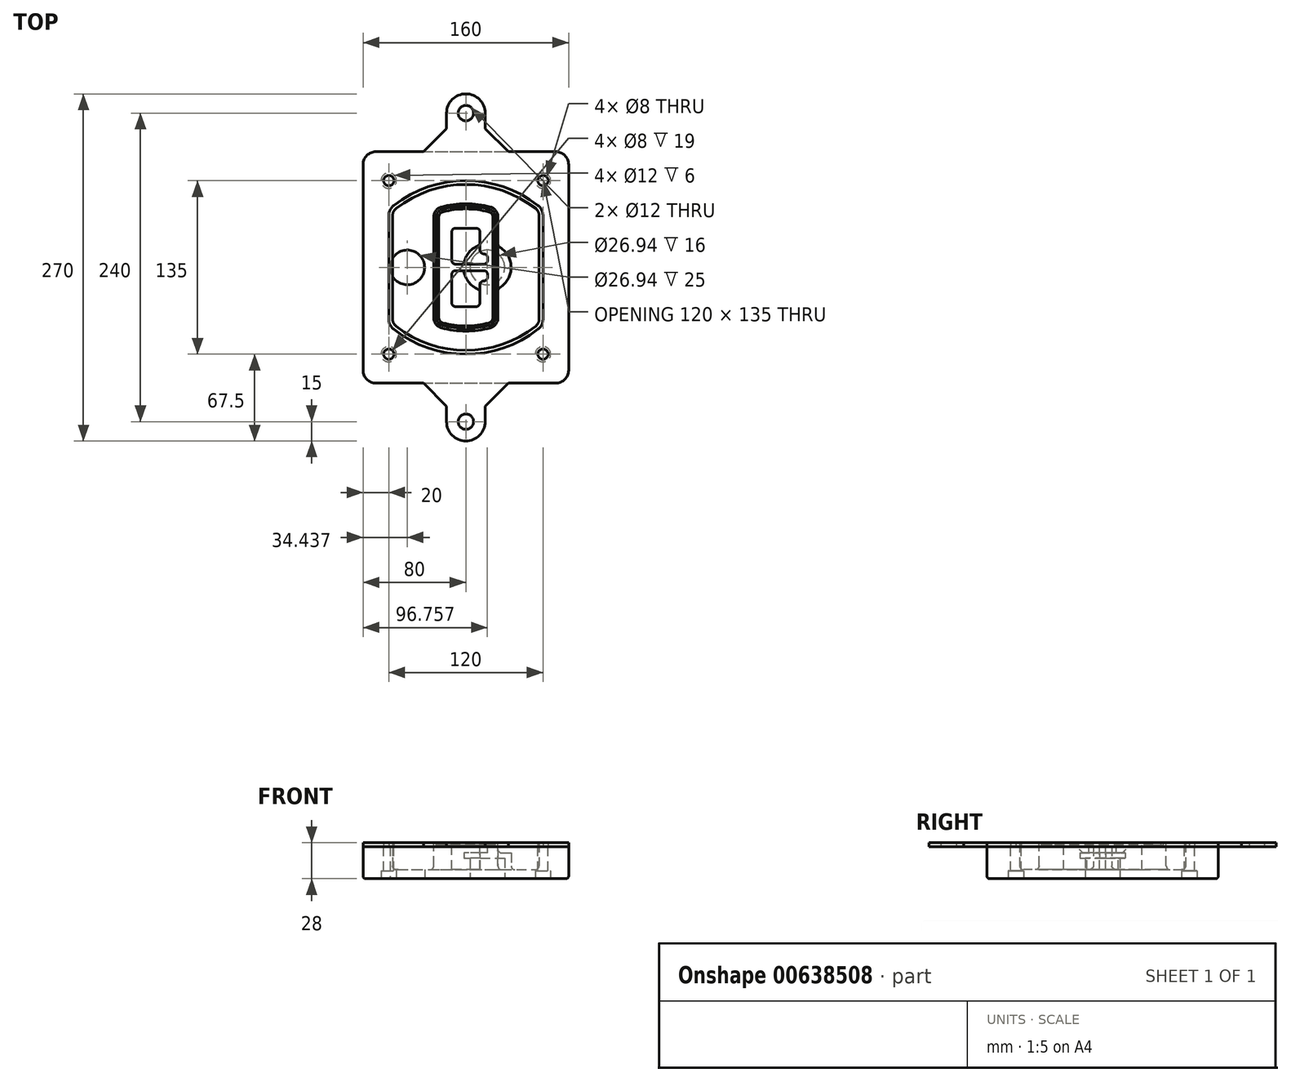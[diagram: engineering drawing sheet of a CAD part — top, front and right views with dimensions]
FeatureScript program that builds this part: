
annotation { "Feature Type Name" : "Feature", "Feature Type Description" : "" }
export const myFeature = defineFeature(function(context is Context, id is Id, definition is map)
    precondition{}
    {
        {
            var Q0;
            Q0=qCreatedBy(makeId("Top.planeOp"),FACE);
            var sketch = newSketch(context, id + "F0", { "sketchPlane" : qUnion([Q0])});
            skPoint(sketch, "E0.rect.middle", {"position": v(0, 0) * mm});
            skLineSegment(sketch, "E1.bottom", {"start": v(-70, -90) * mm, "end": v(70, -90) * mm});
            skLineSegment(sketch, "E1.top", {"start": v(-70, 90) * mm, "end": v(70, 90) * mm});
            skLineSegment(sketch, "E1.left", {"start": v(-80, -80) * mm, "end": v(-80, 80) * mm});
            skLineSegment(sketch, "E1.right", {"start": v(80, -80) * mm, "end": v(80, 80) * mm});
            skLineSegment(sketch, "E2", {"start": v(-80, 90) * mm, "end": v(80, -90) * mm, "construction": true});
            skLineSegment(sketch, "E3", {"start": v(80, 90) * mm, "end": v(-80, -90) * mm, "construction": true});
            skCircle(sketch, "E4", {"center": v(-60, 67.5) * mm, "radius": 4 * mm});
            skCircle(sketch, "E5", {"center": v(60, 67.5) * mm, "radius": 4 * mm});
            skCircle(sketch, "E6", {"center": v(60, -67.5) * mm, "radius": 4 * mm});
            skCircle(sketch, "E7", {"center": v(-60, -67.5) * mm, "radius": 4 * mm});
            skLineSegment(sketch, "E8", {"start": v(-60, 67.5) * mm, "end": v(60, 67.5) * mm, "construction": true});
            skLineSegment(sketch, "E9", {"start": v(60, 67.5) * mm, "end": v(60, -67.5) * mm, "construction": true});
            skLineSegment(sketch, "E10", {"start": v(60, -67.5) * mm, "end": v(-60, -67.5) * mm, "construction": true});
            skLineSegment(sketch, "E11", {"start": v(-60, -67.5) * mm, "end": v(-60, 67.5) * mm, "construction": true});
            skLineSegment(sketch, "E12", {"start": v(-60, 40.3) * mm, "end": v(-60, -40.3) * mm});
            skLineSegment(sketch, "E13", {"start": v(60, 40.3) * mm, "end": v(60, -40.3) * mm});
            skArc(sketch, "E14", {"start": v(56.15, 48.18) * mm, "mid": v(0, 67.5) * mm, "end": v(-56.15, 48.18) * mm});
            skArc(sketch, "E15", {"start": v(-56.15, -48.18) * mm, "mid": v(0, -67.5) * mm, "end": v(56.15, -48.18) * mm});
            skLineSegment(sketch, "E16", {"start": v(-60, 0) * mm, "end": v(60, 0) * mm, "construction": true});
            skPoint(sketch, "E17.visualSharp", {"position": v(-60, -45) * mm});
            skArc(sketch, "E17.filletArc", {"start": v(-60, -40.3) * mm, "mid": v(-58.99, -44.68) * mm, "end": v(-56.15, -48.18) * mm});
            skPoint(sketch, "E18.visualSharp", {"position": v(-60, 45) * mm});
            skArc(sketch, "E18.filletArc", {"start": v(-56.15, 48.18) * mm, "mid": v(-58.99, 44.68) * mm, "end": v(-60, 40.3) * mm});
            skPoint(sketch, "E19.visualSharp", {"position": v(60, 45) * mm});
            skArc(sketch, "E19.filletArc", {"start": v(60, 40.3) * mm, "mid": v(58.99, 44.68) * mm, "end": v(56.15, 48.18) * mm});
            skPoint(sketch, "E20.visualSharp", {"position": v(60, -45) * mm});
            skArc(sketch, "E20.filletArc", {"start": v(56.15, -48.18) * mm, "mid": v(58.99, -44.68) * mm, "end": v(60, -40.3) * mm});
            skPoint(sketch, "E21.visualSharp", {"position": v(-80, 90) * mm});
            skArc(sketch, "E21.filletArc", {"start": v(-70, 90) * mm, "mid": v(-77.07, 87.07) * mm, "end": v(-80, 80) * mm});
            skPoint(sketch, "E22.visualSharp", {"position": v(80, 90) * mm});
            skArc(sketch, "E22.filletArc", {"start": v(80, 80) * mm, "mid": v(77.07, 87.07) * mm, "end": v(70, 90) * mm});
            skPoint(sketch, "E23.visualSharp", {"position": v(80, -90) * mm});
            skArc(sketch, "E23.filletArc", {"start": v(70, -90) * mm, "mid": v(77.07, -87.07) * mm, "end": v(80, -80) * mm});
            skPoint(sketch, "E24.visualSharp", {"position": v(-80, -90) * mm});
            skArc(sketch, "E24.filletArc", {"start": v(-80, -80) * mm, "mid": v(-77.07, -87.07) * mm, "end": v(-70, -90) * mm});
            skArc(sketch, "E25.0", {"start": v(57, 40.3) * mm, "mid": v(56.3, 43.36) * mm, "end": v(54.3, 45.81) * mm});
            skLineSegment(sketch, "E25.1", {"start": v(57, 40.3) * mm, "end": v(57, -40.3) * mm});
            skArc(sketch, "E25.2", {"start": v(54.3, -45.81) * mm, "mid": v(56.3, -43.36) * mm, "end": v(57, -40.3) * mm});
            skArc(sketch, "E25.3", {"start": v(-54.3, -45.81) * mm, "mid": v(0, -64.5) * mm, "end": v(54.3, -45.81) * mm});
            skArc(sketch, "E25.4", {"start": v(-57, -40.3) * mm, "mid": v(-56.3, -43.36) * mm, "end": v(-54.3, -45.81) * mm});
            skArc(sketch, "E25.5", {"start": v(54.3, 45.81) * mm, "mid": v(0, 64.5) * mm, "end": v(-54.3, 45.81) * mm});
            skLineSegment(sketch, "E25.6", {"start": v(-57, 40.3) * mm, "end": v(-57, -40.3) * mm});
            skArc(sketch, "E25.7", {"start": v(-54.3, 45.81) * mm, "mid": v(-56.3, 43.36) * mm, "end": v(-57, 40.3) * mm});
            skArc(sketch, "E26.0", {"start": v(-58.62, 51.33) * mm, "mid": v(-62.58, 46.43) * mm, "end": v(-64, 40.3) * mm});
            skArc(sketch, "E26.1", {"start": v(58.62, 51.33) * mm, "mid": v(0, 71.5) * mm, "end": v(-58.62, 51.33) * mm});
            skArc(sketch, "E26.2", {"start": v(64, 40.3) * mm, "mid": v(62.58, 46.43) * mm, "end": v(58.62, 51.33) * mm});
            skLineSegment(sketch, "E26.3", {"start": v(64, 40.3) * mm, "end": v(64, -40.3) * mm});
            skArc(sketch, "E26.4", {"start": v(58.62, -51.33) * mm, "mid": v(62.58, -46.43) * mm, "end": v(64, -40.3) * mm});
            skLineSegment(sketch, "E26.5", {"start": v(-64, 40.3) * mm, "end": v(-64, -40.3) * mm});
            skArc(sketch, "E26.6", {"start": v(-58.62, -51.33) * mm, "mid": v(0, -71.5) * mm, "end": v(58.62, -51.33) * mm});
            skArc(sketch, "E26.7", {"start": v(-64, -40.3) * mm, "mid": v(-62.58, -46.43) * mm, "end": v(-58.62, -51.33) * mm});
            skSolve(sketch);
        }
        {
            var Q0;
            Q0=makeQuery(id+"F0.imprint","IMPRINT",FACE,{"disambiguationData":[TD([[makeQuery(id+"F0.imprint","IMPRINT",EDGE,{"derivedFrom":sQuery(id+"F0.wireOp",EDGE,"E1.bottom")}),1.0]])]});
            var Q1;
            Q1=makeQuery(id+"F0.imprint","IMPRINT",FACE,{"disambiguationData":[TD([[makeQuery(id+"F0.imprint","IMPRINT",EDGE,{"derivedFrom":sQuery(id+"F0.wireOp",EDGE,"E12")}),1.0]])]});
            var Q2;
            Q2=makeQuery(id+"F0.imprint","IMPRINT",FACE,{"disambiguationData":[TD([[makeQuery(id+"F0.imprint","IMPRINT",EDGE,{"derivedFrom":sQuery(id+"F0.wireOp",EDGE,"E25.0")}),1.0]])]});
            var Q3;
            Q3=makeQuery(id+"F0.imprint","IMPRINT",FACE,{"disambiguationData":[TD([[makeQuery(id+"F0.imprint","IMPRINT",EDGE,{"derivedFrom":sQuery(id+"F0.wireOp",EDGE,"E12")}),-1.0]])]});
            extrude(context, id + "F1", {"entities" : qUnion([Q0, Q1, Q2, Q3]), "oppositeDirection" : true, "depth" : 25 * mm});
        }
        {
            var Q0;
            Q0=makeQuery(id+"F0.imprint","IMPRINT",FACE,{"disambiguationData":[TD([[makeQuery(id+"F0.imprint","IMPRINT",EDGE,{"derivedFrom":sQuery(id+"F0.wireOp",EDGE,"E12")}),1.0]])]});
            extrude(context, id + "F2", {"entities" : qUnion([Q0]), "operationType" : NewBodyOperationType.ADD, "depth" : 3 * mm});
        }
        {
            var Q0;
            Q0=makeQuery(id+"F0.imprint","IMPRINT",FACE,{"disambiguationData":[TD([[makeQuery(id+"F0.imprint","IMPRINT",EDGE,{"derivedFrom":sQuery(id+"F0.wireOp",EDGE,"E25.0")}),1.0]])]});
            extrude(context, id + "F3", {"entities" : qUnion([Q0]), "operationType" : NewBodyOperationType.REMOVE, "oppositeDirection" : true, "depth" : 18 * mm});
        }
        {
            var Q0;
            Q0=makeQuery(id+"F2.opExtrude","CAP_FACE",FACE,{"disambiguationData":[OSD([sQuery(id+"F0.wireOp",EDGE,"E12"),sQuery(id+"F0.wireOp",EDGE,"E13"),sQuery(id+"F0.wireOp",EDGE,"E14"),sQuery(id+"F0.wireOp",EDGE,"E15"),sQuery(id+"F0.wireOp",EDGE,"E17.filletArc"),sQuery(id+"F0.wireOp",EDGE,"E18.filletArc"),sQuery(id+"F0.wireOp",EDGE,"E19.filletArc"),sQuery(id+"F0.wireOp",EDGE,"E20.filletArc"),sQuery(id+"F0.wireOp",EDGE,"E25.0"),sQuery(id+"F0.wireOp",EDGE,"E25.1"),sQuery(id+"F0.wireOp",EDGE,"E25.2"),sQuery(id+"F0.wireOp",EDGE,"E25.3"),sQuery(id+"F0.wireOp",EDGE,"E25.4"),sQuery(id+"F0.wireOp",EDGE,"E25.5"),sQuery(id+"F0.wireOp",EDGE,"E25.6"),sQuery(id+"F0.wireOp",EDGE,"E25.7")])],"isStart":false});
            var sketch = newSketch(context, id + "F4", { "sketchPlane" : qUnion([Q0])});
            skArc(sketch, "E27.0", {"start": v(-19.08, -46.97) * mm, "mid": v(0, -49.5) * mm, "end": v(19.08, -46.97) * mm});
            skArc(sketch, "E28.0", {"start": v(19.08, 46.97) * mm, "mid": v(0, 49.5) * mm, "end": v(-19.08, 46.97) * mm});
            skLineSegment(sketch, "E29", {"start": v(-25, 39.25) * mm, "end": v(-25, -39.25) * mm});
            skLineSegment(sketch, "E30", {"start": v(25, 39.25) * mm, "end": v(25, -39.25) * mm});
            skLineSegment(sketch, "E31", {"start": v(-25, 45.1) * mm, "end": v(25, 45.1) * mm, "construction": true});
            skLineSegment(sketch, "E32", {"start": v(-25, -45.1) * mm, "end": v(25, -45.1) * mm, "construction": true});
            skPoint(sketch, "E33.visualSharp", {"position": v(-25, 45.1) * mm});
            skArc(sketch, "E33.filletArc", {"start": v(-19.08, 46.97) * mm, "mid": v(-23.35, 44.11) * mm, "end": v(-25, 39.25) * mm});
            skPoint(sketch, "E34.visualSharp", {"position": v(25, 45.1) * mm});
            skArc(sketch, "E34.filletArc", {"start": v(25, 39.25) * mm, "mid": v(23.35, 44.11) * mm, "end": v(19.08, 46.97) * mm});
            skPoint(sketch, "E35.visualSharp", {"position": v(25, -45.1) * mm});
            skArc(sketch, "E35.filletArc", {"start": v(19.08, -46.97) * mm, "mid": v(23.35, -44.11) * mm, "end": v(25, -39.25) * mm});
            skPoint(sketch, "E36.visualSharp", {"position": v(-25, -45.1) * mm});
            skArc(sketch, "E36.filletArc", {"start": v(-25, -39.25) * mm, "mid": v(-23.35, -44.11) * mm, "end": v(-19.08, -46.97) * mm});
            skArc(sketch, "E37.0", {"start": v(54.3, 45.81) * mm, "mid": v(0, 64.5) * mm, "end": v(-54.3, 45.81) * mm});
            skArc(sketch, "E37.1", {"start": v(-54.3, 45.81) * mm, "mid": v(-56.3, 43.36) * mm, "end": v(-57, 40.3) * mm});
            skLineSegment(sketch, "E37.2", {"start": v(-57, 40.3) * mm, "end": v(-57, -40.3) * mm});
            skArc(sketch, "E37.3", {"start": v(-57, -40.3) * mm, "mid": v(-56.3, -43.36) * mm, "end": v(-54.3, -45.81) * mm});
            skArc(sketch, "E37.4", {"start": v(-54.3, -45.81) * mm, "mid": v(0, -64.5) * mm, "end": v(54.3, -45.81) * mm});
            skArc(sketch, "E37.5", {"start": v(54.3, -45.81) * mm, "mid": v(56.3, -43.36) * mm, "end": v(57, -40.3) * mm});
            skLineSegment(sketch, "E37.6", {"start": v(57, 40.3) * mm, "end": v(57, -40.3) * mm});
            skArc(sketch, "E37.7", {"start": v(57, 40.3) * mm, "mid": v(56.3, 43.36) * mm, "end": v(54.3, 45.81) * mm});
            skLineSegment(sketch, "E38.0", {"start": v(23, 39.25) * mm, "end": v(23, -39.25) * mm});
            skArc(sketch, "E38.1", {"start": v(18.56, -45.04) * mm, "mid": v(21.76, -42.9) * mm, "end": v(23, -39.25) * mm});
            skArc(sketch, "E38.2", {"start": v(-18.56, -45.04) * mm, "mid": v(0, -47.5) * mm, "end": v(18.56, -45.04) * mm});
            skArc(sketch, "E38.3", {"start": v(-23, -39.25) * mm, "mid": v(-21.76, -42.9) * mm, "end": v(-18.56, -45.04) * mm});
            skLineSegment(sketch, "E38.4", {"start": v(-23, 39.25) * mm, "end": v(-23, -39.25) * mm});
            skArc(sketch, "E38.5", {"start": v(23, 39.25) * mm, "mid": v(21.76, 42.9) * mm, "end": v(18.56, 45.04) * mm});
            skArc(sketch, "E38.6", {"start": v(-18.56, 45.04) * mm, "mid": v(-21.76, 42.9) * mm, "end": v(-23, 39.25) * mm});
            skArc(sketch, "E38.7", {"start": v(18.56, 45.04) * mm, "mid": v(0, 47.5) * mm, "end": v(-18.56, 45.04) * mm});
            skArc(sketch, "E39.0", {"start": v(21, 39.25) * mm, "mid": v(20.18, 41.68) * mm, "end": v(18.04, 43.1) * mm});
            skLineSegment(sketch, "E39.1", {"start": v(21, 39.25) * mm, "end": v(21, -39.25) * mm});
            skArc(sketch, "E39.2", {"start": v(18.04, -43.1) * mm, "mid": v(20.18, -41.68) * mm, "end": v(21, -39.25) * mm});
            skArc(sketch, "E39.3", {"start": v(-18.04, -43.1) * mm, "mid": v(0, -45.5) * mm, "end": v(18.04, -43.1) * mm});
            skArc(sketch, "E39.4", {"start": v(-21, -39.25) * mm, "mid": v(-20.18, -41.68) * mm, "end": v(-18.04, -43.1) * mm});
            skArc(sketch, "E39.5", {"start": v(18.04, 43.1) * mm, "mid": v(0, 45.5) * mm, "end": v(-18.04, 43.1) * mm});
            skLineSegment(sketch, "E39.6", {"start": v(-21, 39.25) * mm, "end": v(-21, -39.25) * mm});
            skArc(sketch, "E39.7", {"start": v(-18.04, 43.1) * mm, "mid": v(-20.18, 41.68) * mm, "end": v(-21, 39.25) * mm});
            skLineSegment(sketch, "E40", {"start": v(-25, 0) * mm, "end": v(25, 0) * mm, "construction": true});
            skLineSegment(sketch, "E41", {"start": v(-11, 5.5) * mm, "end": v(-11, 27.5) * mm});
            skLineSegment(sketch, "E42", {"start": v(-8, 30.5) * mm, "end": v(8, 30.5) * mm});
            skLineSegment(sketch, "E43", {"start": v(11, 27.5) * mm, "end": v(11, 13.5) * mm});
            skLineSegment(sketch, "E44", {"start": v(14, 10.5) * mm, "end": v(14, 10.5) * mm});
            skLineSegment(sketch, "E45", {"start": v(17, 7.5) * mm, "end": v(17, 5.5) * mm});
            skLineSegment(sketch, "E46", {"start": v(14, 2.5) * mm, "end": v(-8, 2.5) * mm});
            skPoint(sketch, "E47.visualSharp", {"position": v(-11, 30.5) * mm});
            skArc(sketch, "E47.filletArc", {"start": v(-8, 30.5) * mm, "mid": v(-10.12, 29.62) * mm, "end": v(-11, 27.5) * mm});
            skPoint(sketch, "E48.visualSharp", {"position": v(11, 30.5) * mm});
            skArc(sketch, "E48.filletArc", {"start": v(11, 27.5) * mm, "mid": v(10.12, 29.62) * mm, "end": v(8, 30.5) * mm});
            skPoint(sketch, "E49.visualSharp", {"position": v(11, 10.5) * mm});
            skArc(sketch, "E49.filletArc", {"start": v(11, 13.5) * mm, "mid": v(11.88, 11.38) * mm, "end": v(14, 10.5) * mm});
            skPoint(sketch, "E50.visualSharp", {"position": v(17, 10.5) * mm});
            skArc(sketch, "E50.filletArc", {"start": v(17, 7.5) * mm, "mid": v(16.12, 9.62) * mm, "end": v(14, 10.5) * mm});
            skPoint(sketch, "E51.visualSharp", {"position": v(17, 2.5) * mm});
            skArc(sketch, "E51.filletArc", {"start": v(14, 2.5) * mm, "mid": v(16.12, 3.38) * mm, "end": v(17, 5.5) * mm});
            skPoint(sketch, "E52.visualSharp", {"position": v(-11, 2.5) * mm});
            skArc(sketch, "E52.filletArc", {"start": v(-11, 5.5) * mm, "mid": v(-10.12, 3.38) * mm, "end": v(-8, 2.5) * mm});
            skLineSegment(sketch, "E53.0.MirrorCS", {"start": v(14, -2.5) * mm, "end": v(-8, -2.5) * mm});
            skArc(sketch, "E54.0.MirrorCS", {"start": v(-11, -5.5) * mm, "mid": v(-10.12, -3.38) * mm, "end": v(-8, -2.5) * mm});
            skLineSegment(sketch, "E55.0.MirrorCS", {"start": v(-11, -5.5) * mm, "end": v(-11, -27.5) * mm});
            skArc(sketch, "E56.0.MirrorCS", {"start": v(-8, -30.5) * mm, "mid": v(-10.12, -29.62) * mm, "end": v(-11, -27.5) * mm});
            skLineSegment(sketch, "E57.0.MirrorCS", {"start": v(-8, -30.5) * mm, "end": v(8, -30.5) * mm});
            skArc(sketch, "E58.0.MirrorCS", {"start": v(11, -27.5) * mm, "mid": v(10.12, -29.62) * mm, "end": v(8, -30.5) * mm});
            skLineSegment(sketch, "E59.0.MirrorCS", {"start": v(11, -27.5) * mm, "end": v(11, -13.5) * mm});
            skArc(sketch, "E60.0.MirrorCS", {"start": v(11, -13.5) * mm, "mid": v(11.88, -11.38) * mm, "end": v(14, -10.5) * mm});
            skArc(sketch, "E61.0.MirrorCS", {"start": v(17, -7.5) * mm, "mid": v(16.12, -9.62) * mm, "end": v(14, -10.5) * mm});
            skLineSegment(sketch, "E62.0.MirrorCS", {"start": v(17, -7.5) * mm, "end": v(17, -5.5) * mm});
            skArc(sketch, "E63.0.MirrorCS", {"start": v(14, -2.5) * mm, "mid": v(16.12, -3.38) * mm, "end": v(17, -5.5) * mm});
            skSolve(sketch);
        }
        {
            var Q0;
            Q0=makeQuery(id+"F4.imprint","IMPRINT",FACE,{"disambiguationData":[TD([[makeQuery(id+"F4.imprint","IMPRINT",EDGE,{"derivedFrom":sQuery(id+"F4.wireOp",EDGE,"E27.0")}),1.0]])]});
            var Q1;
            Q1=makeQuery(id+"F4.imprint","IMPRINT",FACE,{"disambiguationData":[TD([[makeQuery(id+"F4.imprint","IMPRINT",EDGE,{"derivedFrom":sQuery(id+"F4.wireOp",EDGE,"E38.0")}),-1.0]])]});
            var Q2;
            Q2=makeQuery(id+"F4.imprint","IMPRINT",FACE,{"disambiguationData":[TD([[makeQuery(id+"F4.imprint","IMPRINT",EDGE,{"derivedFrom":sQuery(id+"F4.wireOp",EDGE,"E39.0")}),1.0]])]});
            extrude(context, id + "F5", {"entities" : qUnion([Q0, Q1, Q2]), "operationType" : NewBodyOperationType.ADD, "endBound" : BoundingType.UP_TO_NEXT, "oppositeDirection" : true, "depth" : 25 * mm});
        }
        {
            var Q0;
            Q0=makeQuery(id+"F4.imprint","IMPRINT",FACE,{"disambiguationData":[TD([[makeQuery(id+"F4.imprint","IMPRINT",EDGE,{"derivedFrom":sQuery(id+"F4.wireOp",EDGE,"E38.0")}),-1.0]])]});
            extrude(context, id + "F6", {"entities" : qUnion([Q0]), "operationType" : NewBodyOperationType.REMOVE, "oppositeDirection" : true, "depth" : 2 * mm});
        }
        {
            var Q0;
            Q0=makeQuery(id+"F1.opExtrude","CAP_FACE",FACE,{"disambiguationData":[OSD([sQuery(id+"F0.wireOp",EDGE,"E1.bottom"),sQuery(id+"F0.wireOp",EDGE,"E1.top"),sQuery(id+"F0.wireOp",EDGE,"E1.left"),sQuery(id+"F0.wireOp",EDGE,"E1.right"),sQuery(id+"F0.wireOp",EDGE,"E4"),sQuery(id+"F0.wireOp",EDGE,"E5"),sQuery(id+"F0.wireOp",EDGE,"E6"),sQuery(id+"F0.wireOp",EDGE,"E7"),sQuery(id+"F0.wireOp",EDGE,"E21.filletArc"),sQuery(id+"F0.wireOp",EDGE,"E22.filletArc"),sQuery(id+"F0.wireOp",EDGE,"E23.filletArc"),sQuery(id+"F0.wireOp",EDGE,"E24.filletArc")])],"isStart":false});
            var sketch = newSketch(context, id + "F7", { "sketchPlane" : qUnion([Q0])});
            skCircle(sketch, "E64", {"center": v(16.76, 0) * mm, "radius": 13.47 * mm});
            skCircle(sketch, "E65", {"center": v(-45.56, 0) * mm, "radius": 13.47 * mm});
            skLineSegment(sketch, "E66", {"start": v(80, 0) * mm, "end": v(-80, 0) * mm});
            skCircle(sketch, "E67", {"center": v(16.76, 0) * mm, "radius": 18.47 * mm});
            skCircle(sketch, "E68", {"center": v(60, -67.5) * mm, "radius": 6 * mm});
            skCircle(sketch, "E69", {"center": v(-60, -67.5) * mm, "radius": 6 * mm});
            skCircle(sketch, "E70", {"center": v(-60, 67.5) * mm, "radius": 6 * mm});
            skCircle(sketch, "E71", {"center": v(60, 67.5) * mm, "radius": 6 * mm});
            skSolve(sketch);
        }
        {
            var Q0;
            {var subQ1=sQuery(id+"F7.wireOp",EDGE,"E66");var subQ4=sQuery(id+"F7.wireOp",EDGE,"E64");var subQ6=makeQuery(id+"F7.imprint","INTERSECT",VERTEX,{"disambiguationData":[OD(0.0)],"derivedFrom":[subQ4,subQ1]});Q0=makeQuery(id+"F7.imprint","IMPRINT",FACE,{"disambiguationData":[TD([[makeQuery(id+"F7.imprint","IMPRINT",EDGE,{"disambiguationData":[TD([[subQ6,-1.0]])],"derivedFrom":subQ4}),-1.0]])]});}
            var Q1;
            {var subQ0=sQuery(id+"F7.wireOp",EDGE,"E66");var subQ1=sQuery(id+"F7.wireOp",EDGE,"E64");var subQ3=makeQuery(id+"F7.imprint","INTERSECT",VERTEX,{"disambiguationData":[OD(0.0)],"derivedFrom":[subQ1,subQ0]});Q1=makeQuery(id+"F7.imprint","IMPRINT",FACE,{"disambiguationData":[TD([[makeQuery(id+"F7.imprint","IMPRINT",EDGE,{"disambiguationData":[TD([[subQ3,-1.0]])],"derivedFrom":subQ1}),1.0]])]});}
            var Q2;
            {var subQ0=sQuery(id+"F7.wireOp",EDGE,"E66");var subQ1=sQuery(id+"F7.wireOp",EDGE,"E64");var subQ3=makeQuery(id+"F7.imprint","INTERSECT",VERTEX,{"disambiguationData":[OD(0.0)],"derivedFrom":[subQ1,subQ0]});Q2=makeQuery(id+"F7.imprint","IMPRINT",FACE,{"disambiguationData":[TD([[makeQuery(id+"F7.imprint","IMPRINT",EDGE,{"disambiguationData":[TD([[subQ3,1.0]])],"derivedFrom":subQ1}),1.0]])]});}
            var Q3;
            {var subQ1=sQuery(id+"F7.wireOp",EDGE,"E66");var subQ4=sQuery(id+"F7.wireOp",EDGE,"E64");var subQ6=makeQuery(id+"F7.imprint","INTERSECT",VERTEX,{"disambiguationData":[OD(0.0)],"derivedFrom":[subQ4,subQ1]});Q3=makeQuery(id+"F7.imprint","IMPRINT",FACE,{"disambiguationData":[TD([[makeQuery(id+"F7.imprint","IMPRINT",EDGE,{"disambiguationData":[TD([[subQ6,1.0]])],"derivedFrom":subQ4}),-1.0]])]});}
            extrude(context, id + "F8", {"entities" : qUnion([Q0, Q1, Q2, Q3]), "operationType" : NewBodyOperationType.ADD, "oppositeDirection" : true, "depth" : 20 * mm});
        }
        {
            var Q0;
            {var subQ0=sQuery(id+"F7.wireOp",EDGE,"E66");var subQ1=sQuery(id+"F7.wireOp",EDGE,"E64");var subQ3=makeQuery(id+"F7.imprint","INTERSECT",VERTEX,{"disambiguationData":[OD(0.0)],"derivedFrom":[subQ1,subQ0]});Q0=makeQuery(id+"F7.imprint","IMPRINT",FACE,{"disambiguationData":[TD([[makeQuery(id+"F7.imprint","IMPRINT",EDGE,{"disambiguationData":[TD([[subQ3,-1.0]])],"derivedFrom":subQ1}),1.0]])]});}
            var Q1;
            {var subQ0=sQuery(id+"F7.wireOp",EDGE,"E66");var subQ1=sQuery(id+"F7.wireOp",EDGE,"E64");var subQ3=makeQuery(id+"F7.imprint","INTERSECT",VERTEX,{"disambiguationData":[OD(0.0)],"derivedFrom":[subQ1,subQ0]});Q1=makeQuery(id+"F7.imprint","IMPRINT",FACE,{"disambiguationData":[TD([[makeQuery(id+"F7.imprint","IMPRINT",EDGE,{"disambiguationData":[TD([[subQ3,1.0]])],"derivedFrom":subQ1}),1.0]])]});}
            extrude(context, id + "F9", {"entities" : qUnion([Q0, Q1]), "operationType" : NewBodyOperationType.REMOVE, "oppositeDirection" : true, "depth" : 16 * mm});
        }
        {
            var Q0;
            {var subQ0=sQuery(id+"F7.wireOp",EDGE,"E66");var subQ1=sQuery(id+"F7.wireOp",EDGE,"E65");var subQ3=makeQuery(id+"F7.imprint","INTERSECT",VERTEX,{"disambiguationData":[OD(0.0)],"derivedFrom":[subQ1,subQ0]});Q0=makeQuery(id+"F7.imprint","IMPRINT",FACE,{"disambiguationData":[TD([[makeQuery(id+"F7.imprint","IMPRINT",EDGE,{"disambiguationData":[TD([[subQ3,-1.0]])],"derivedFrom":subQ1}),1.0]])]});}
            var Q1;
            {var subQ0=sQuery(id+"F7.wireOp",EDGE,"E66");var subQ1=sQuery(id+"F7.wireOp",EDGE,"E65");var subQ3=makeQuery(id+"F7.imprint","INTERSECT",VERTEX,{"disambiguationData":[OD(0.0)],"derivedFrom":[subQ1,subQ0]});Q1=makeQuery(id+"F7.imprint","IMPRINT",FACE,{"disambiguationData":[TD([[makeQuery(id+"F7.imprint","IMPRINT",EDGE,{"disambiguationData":[TD([[subQ3,1.0]])],"derivedFrom":subQ1}),1.0]])]});}
            extrude(context, id + "F10", {"entities" : qUnion([Q0, Q1]), "operationType" : NewBodyOperationType.REMOVE, "oppositeDirection" : true, "depth" : 25 * mm});
        }
        {
            var Q0;
            Q0=makeQuery(id+"F7.imprint","IMPRINT",FACE,{"disambiguationData":[TD([[makeQuery(id+"F7.imprint","IMPRINT",EDGE,{"derivedFrom":sQuery(id+"F7.wireOp",EDGE,"E68")}),1.0]])]});
            var Q1;
            Q1=makeQuery(id+"F7.imprint","IMPRINT",FACE,{"disambiguationData":[TD([[makeQuery(id+"F7.imprint","IMPRINT",EDGE,{"derivedFrom":makeQuery(id+"F1.opExtrude","CAP_EDGE",EDGE,{"disambiguationData":[OSD([sQuery(id+"F0.wireOp",EDGE,"E5")])],"isStart":false})}),-1.0]])]});
            var Q2;
            Q2=makeQuery(id+"F7.imprint","IMPRINT",FACE,{"disambiguationData":[TD([[makeQuery(id+"F7.imprint","IMPRINT",EDGE,{"derivedFrom":sQuery(id+"F7.wireOp",EDGE,"E69")}),1.0]])]});
            var Q3;
            Q3=makeQuery(id+"F7.imprint","IMPRINT",FACE,{"disambiguationData":[TD([[makeQuery(id+"F7.imprint","IMPRINT",EDGE,{"derivedFrom":makeQuery(id+"F1.opExtrude","CAP_EDGE",EDGE,{"disambiguationData":[OSD([sQuery(id+"F0.wireOp",EDGE,"E4")])],"isStart":false})}),-1.0]])]});
            var Q4;
            Q4=makeQuery(id+"F7.imprint","IMPRINT",FACE,{"disambiguationData":[TD([[makeQuery(id+"F7.imprint","IMPRINT",EDGE,{"derivedFrom":sQuery(id+"F7.wireOp",EDGE,"E70")}),1.0]])]});
            var Q5;
            Q5=makeQuery(id+"F7.imprint","IMPRINT",FACE,{"disambiguationData":[TD([[makeQuery(id+"F7.imprint","IMPRINT",EDGE,{"derivedFrom":makeQuery(id+"F1.opExtrude","CAP_EDGE",EDGE,{"disambiguationData":[OSD([sQuery(id+"F0.wireOp",EDGE,"E7")])],"isStart":false})}),-1.0]])]});
            var Q6;
            Q6=makeQuery(id+"F7.imprint","IMPRINT",FACE,{"disambiguationData":[TD([[makeQuery(id+"F7.imprint","IMPRINT",EDGE,{"derivedFrom":sQuery(id+"F7.wireOp",EDGE,"E71")}),1.0]])]});
            var Q7;
            Q7=makeQuery(id+"F7.imprint","IMPRINT",FACE,{"disambiguationData":[TD([[makeQuery(id+"F7.imprint","IMPRINT",EDGE,{"derivedFrom":makeQuery(id+"F1.opExtrude","CAP_EDGE",EDGE,{"disambiguationData":[OSD([sQuery(id+"F0.wireOp",EDGE,"E6")])],"isStart":false})}),-1.0]])]});
            extrude(context, id + "F11", {"entities" : qUnion([Q0, Q1, Q2, Q3, Q4, Q5, Q6, Q7]), "operationType" : NewBodyOperationType.REMOVE, "oppositeDirection" : true, "depth" : 6 * mm});
        }
        {
            var Q0;
            Q0=makeQuery(id+"F9.boolean.opBoolean","COPY",FACE,{"derivedFrom":makeQuery(id+"F9.opExtrude","CAP_FACE",FACE,{"disambiguationData":[OSD([sQuery(id+"F7.wireOp",EDGE,"E64")])],"isStart":false})});
            var sketch = newSketch(context, id + "F12", { "sketchPlane" : qUnion([Q0])});
            skArc(sketch, "E72.0", {"start": v(11, 17.55) * mm, "mid": v(2.57, 11.82) * mm, "end": v(-1.54, 2.5) * mm});
            skArc(sketch, "E72.1", {"start": v(-1.54, -2.5) * mm, "mid": v(2.57, -11.82) * mm, "end": v(11, -17.55) * mm});
            skLineSegment(sketch, "E73", {"start": v(-1.54, -2.5) * mm, "end": v(14, -2.5) * mm});
            skLineSegment(sketch, "E74.0", {"start": v(14, 2.5) * mm, "end": v(-1.54, 2.5) * mm});
            skArc(sketch, "E74.1", {"start": v(14, 2.5) * mm, "mid": v(16.12, 3.38) * mm, "end": v(17, 5.5) * mm});
            skLineSegment(sketch, "E74.2", {"start": v(17, 7.5) * mm, "end": v(17, 5.5) * mm});
            skArc(sketch, "E74.3", {"start": v(17, 7.5) * mm, "mid": v(16.12, 9.62) * mm, "end": v(14, 10.5) * mm});
            skArc(sketch, "E74.4", {"start": v(11, 13.5) * mm, "mid": v(11.88, 11.38) * mm, "end": v(14, 10.5) * mm});
            skLineSegment(sketch, "E74.5", {"start": v(11, 17.55) * mm, "end": v(11, 13.5) * mm});
            skLineSegment(sketch, "E74.7", {"start": v(14, -2.5) * mm, "end": v(-1.54, -2.5) * mm});
            skArc(sketch, "E74.8", {"start": v(14, -2.5) * mm, "mid": v(16.12, -3.38) * mm, "end": v(17, -5.5) * mm});
            skLineSegment(sketch, "E74.9", {"start": v(17, -7.5) * mm, "end": v(17, -5.5) * mm});
            skArc(sketch, "E74.10", {"start": v(17, -7.5) * mm, "mid": v(16.12, -9.62) * mm, "end": v(14, -10.5) * mm});
            skArc(sketch, "E74.11", {"start": v(11, -13.5) * mm, "mid": v(11.88, -11.38) * mm, "end": v(14, -10.5) * mm});
            skLineSegment(sketch, "E74.12", {"start": v(11, -17.55) * mm, "end": v(11, -13.5) * mm});
            skPoint(sketch, "E75.orphan", {"position": v(11, -27.5) * mm});
            skPoint(sketch, "E76.orphan", {"position": v(-8, -2.5) * mm});
            skPoint(sketch, "E77.orphan", {"position": v(-8, 2.5) * mm});
            skPoint(sketch, "E78.orphan", {"position": v(11, 27.5) * mm});
            skSolve(sketch);
        }
        {
            var Q0;
            {var subQ7=sQuery(id+"F12.wireOp",EDGE,"E72.0");var subQ14=sQuery(id+"F12.wireOp",EDGE,"E72.1");var subQ16=sQuery(id+"F12.wireOp",EDGE,"E74.1");var subQ18=sQuery(id+"F12.wireOp",EDGE,"E74.8");Q0=qUnion([makeQuery(id+"F12.imprint","IMPRINT",FACE,{"disambiguationData":[TD([[makeQuery(id+"F12.imprint","IMPRINT",EDGE,{"derivedFrom":subQ7}),1.0]])]}),makeQuery(id+"F12.imprint","IMPRINT",FACE,{"disambiguationData":[TD([[makeQuery(id+"F12.imprint","IMPRINT",EDGE,{"derivedFrom":subQ14}),1.0]])]}),makeQuery(id+"F12.imprint","IMPRINT",FACE,{"disambiguationData":[TD([[makeQuery(id+"F12.imprint","IMPRINT",EDGE,{"derivedFrom":subQ16}),1.0]])]}),makeQuery(id+"F12.imprint","IMPRINT",FACE,{"disambiguationData":[TD([[makeQuery(id+"F12.imprint","IMPRINT",EDGE,{"derivedFrom":subQ18}),-1.0]])]})]);}
            var Q1;
            Q1=makeQuery(id+"F5.boolean.opBoolean","SPLIT",FACE,{"disambiguationData":[TD([makeQuery(id+"F5.opExtrude","SWEPT_FACE",FACE,{"disambiguationData":[OSD([sQuery(id+"F4.wireOp",EDGE,"E41")])]})])],"derivedFrom":makeQuery(id+"F3.boolean.opBoolean","COPY",FACE,{"derivedFrom":makeQuery(id+"F3.opExtrude","CAP_FACE",FACE,{"disambiguationData":[OSD([sQuery(id+"F0.wireOp",EDGE,"E25.0"),sQuery(id+"F0.wireOp",EDGE,"E25.1"),sQuery(id+"F0.wireOp",EDGE,"E25.2"),sQuery(id+"F0.wireOp",EDGE,"E25.3"),sQuery(id+"F0.wireOp",EDGE,"E25.4"),sQuery(id+"F0.wireOp",EDGE,"E25.5"),sQuery(id+"F0.wireOp",EDGE,"E25.6"),sQuery(id+"F0.wireOp",EDGE,"E25.7")])],"isStart":false})})});
            extrude(context, id + "F13", {"entities" : qUnion([Q0]), "operationType" : NewBodyOperationType.REMOVE, "endBound" : BoundingType.UP_TO_SURFACE, "endBoundEntityFace" : qUnion([Q1]), "depth" : 25 * mm});
        }
        {
            var Q0;
            Q0=makeQuery(id+"F3.boolean.opBoolean","COPY",EDGE,{"derivedFrom":makeQuery(id+"F3.opExtrude","CAP_EDGE",EDGE,{"disambiguationData":[OSD([sQuery(id+"F0.wireOp",EDGE,"E25.6")])],"isStart":false})});
            var Q1;
            Q1=makeQuery(id+"F8.boolean.opBoolean","INTERSECT",EDGE,{"derivedFrom":[makeQuery(id+"F5.opExtrude","SWEPT_FACE",FACE,{"disambiguationData":[OSD([sQuery(id+"F4.wireOp",EDGE,"E30")])]}),makeQuery(id+"F8.opExtrude","CAP_FACE",FACE,{"disambiguationData":[OSD([sQuery(id+"F7.wireOp",EDGE,"E67")])],"isStart":false})]});
            var Q2;
            Q2=makeQuery(id+"F8.boolean.opBoolean","INTERSECT",EDGE,{"disambiguationData":[OD(1.0)],"derivedFrom":[makeQuery(id+"F5.opExtrude","SWEPT_FACE",FACE,{"disambiguationData":[OSD([sQuery(id+"F4.wireOp",EDGE,"E30")])]}),makeQuery(id+"F8.opExtrude","SWEPT_FACE",FACE,{"disambiguationData":[OSD([sQuery(id+"F7.wireOp",EDGE,"E67")])]})]});
            var Q3;
            {var subQ0=sQuery(id+"F4.wireOp",EDGE,"E30");Q3=makeQuery(id+"F8.boolean.opBoolean","SPLIT",EDGE,{"disambiguationData":[TD([makeQuery(id+"F5.opExtrude","SWEPT_FACE",FACE,{"disambiguationData":[OSD([sQuery(id+"F4.wireOp",EDGE,"E35.filletArc")])]})])],"derivedFrom":makeQuery(id+"F5.opExtrude","CAP_EDGE",EDGE,{"disambiguationData":[OSD([subQ0])],"isStart":false})});}
            var Q4;
            {var subQ0=sQuery(id+"F0.wireOp",EDGE,"E25.7");var subQ1=sQuery(id+"F0.wireOp",EDGE,"E25.1");var subQ2=sQuery(id+"F0.wireOp",EDGE,"E25.6");var subQ3=sQuery(id+"F0.wireOp",EDGE,"E25.5");var subQ4=sQuery(id+"F0.wireOp",EDGE,"E25.4");var subQ5=sQuery(id+"F0.wireOp",EDGE,"E25.0");var subQ6=sQuery(id+"F0.wireOp",EDGE,"E25.2");var subQ7=sQuery(id+"F0.wireOp",EDGE,"E25.3");Q4=makeQuery(id+"F8.boolean.opBoolean","INTERSECT",EDGE,{"derivedFrom":[makeQuery(id+"F5.boolean.opBoolean","SPLIT",FACE,{"disambiguationData":[TD([makeQuery(id+"F2.opExtrude","SWEPT_FACE",FACE,{"disambiguationData":[OSD([subQ5])]})])],"derivedFrom":makeQuery(id+"F3.boolean.opBoolean","COPY",FACE,{"derivedFrom":makeQuery(id+"F3.opExtrude","CAP_FACE",FACE,{"disambiguationData":[OSD([subQ5,subQ1,subQ6,subQ7,subQ4,subQ3,subQ2,subQ0])],"isStart":false})})}),makeQuery(id+"F8.opExtrude","SWEPT_FACE",FACE,{"disambiguationData":[OSD([sQuery(id+"F7.wireOp",EDGE,"E67")])]})]});}
            var Q5;
            Q5=makeQuery(id+"F8.boolean.opBoolean","INTERSECT",EDGE,{"disambiguationData":[OD(0.0)],"derivedFrom":[makeQuery(id+"F5.opExtrude","SWEPT_FACE",FACE,{"disambiguationData":[OSD([sQuery(id+"F4.wireOp",EDGE,"E30")])]}),makeQuery(id+"F8.opExtrude","SWEPT_FACE",FACE,{"disambiguationData":[OSD([sQuery(id+"F7.wireOp",EDGE,"E67")])]})]});
            fillet(context, id + "F14", {"entities" : qUnion([Q0, Q1, Q2, Q3, Q4, Q5]), "radius" : 3 * mm, "tangentPropagation" : true, "allowEdgeOverflow" : false});
        }
        {
            var Q0;
            Q0=makeQuery(id+"F1.opExtrude","CAP_EDGE",EDGE,{"disambiguationData":[OSD([sQuery(id+"F0.wireOp",EDGE,"E1.bottom")])],"isStart":false});
            fillet(context, id + "F15", {"entities" : qUnion([Q0]), "radius" : 2 * mm, "tangentPropagation" : true, "allowEdgeOverflow" : false});
        }
        {
            var Q0;
            {var subQ0=sQuery(id+"F0.wireOp",EDGE,"E21.filletArc");var subQ1=sQuery(id+"F0.wireOp",EDGE,"E7");var subQ2=sQuery(id+"F0.wireOp",EDGE,"E6");var subQ3=sQuery(id+"F0.wireOp",EDGE,"E5");var subQ4=sQuery(id+"F0.wireOp",EDGE,"E4");var subQ5=sQuery(id+"F0.wireOp",EDGE,"E22.filletArc");var subQ6=sQuery(id+"F0.wireOp",EDGE,"E1.bottom");var subQ7=sQuery(id+"F0.wireOp",EDGE,"E1.right");var subQ8=sQuery(id+"F0.wireOp",EDGE,"E1.top");var subQ9=sQuery(id+"F0.wireOp",EDGE,"E1.left");var subQ10=sQuery(id+"F0.wireOp",EDGE,"E23.filletArc");var subQ11=sQuery(id+"F0.wireOp",EDGE,"E24.filletArc");Q0=makeQuery(id+"F2.boolean.opBoolean","SPLIT",FACE,{"disambiguationData":[TD([makeQuery(id+"F1.opExtrude","SWEPT_FACE",FACE,{"disambiguationData":[OSD([subQ6])]})])],"derivedFrom":makeQuery(id+"F1.opExtrude","CAP_FACE",FACE,{"disambiguationData":[OSD([subQ6,subQ8,subQ9,subQ7,subQ4,subQ3,subQ2,subQ1,subQ0,subQ5,subQ10,subQ11])],"isStart":true})});}
            var sketch = newSketch(context, id + "F16", { "sketchPlane" : qUnion([Q0])});
            skCircle(sketch, "E79", {"center": v(0, 120) * mm, "radius": 6 * mm});
            skPoint(sketch, "E79.first.point", {"position": v(-3.45, 115.09) * mm});
            skArc(sketch, "E80", {"start": v(15, 120) * mm, "mid": v(0, 135) * mm, "end": v(-15, 120) * mm});
            skLineSegment(sketch, "E81", {"start": v(0, 90) * mm, "end": v(0, 120) * mm, "construction": true});
            skLineSegment(sketch, "E82", {"start": v(-33, 90) * mm, "end": v(-15, 108) * mm});
            skLineSegment(sketch, "E83", {"start": v(-15, 108) * mm, "end": v(-15, 120) * mm});
            skLineSegment(sketch, "E84", {"start": v(15, 120) * mm, "end": v(15, 108) * mm});
            skLineSegment(sketch, "E85", {"start": v(-15, 120) * mm, "end": v(15, 120) * mm, "construction": true});
            skLineSegment(sketch, "E86", {"start": v(15, 108) * mm, "end": v(33, 90) * mm});
            skLineSegment(sketch, "E87", {"start": v(-80, 0) * mm, "end": v(80, 0) * mm, "construction": true});
            skLineSegment(sketch, "E88.MirrorCS", {"start": v(15, -108) * mm, "end": v(33, -90) * mm});
            skLineSegment(sketch, "E89.MirrorCS", {"start": v(15, -120) * mm, "end": v(15, -108) * mm});
            skLineSegment(sketch, "E90.MirrorCS", {"start": v(-15, -120) * mm, "end": v(15, -120) * mm, "construction": true});
            skLineSegment(sketch, "E91.MirrorCS", {"start": v(0, -90) * mm, "end": v(0, -120) * mm, "construction": true});
            skArc(sketch, "E92.MirrorCS", {"start": v(15, -120) * mm, "mid": v(0, -135) * mm, "end": v(-15, -120) * mm});
            skCircle(sketch, "E93.MirrorC", {"center": v(0, -120) * mm, "radius": 6 * mm});
            skLineSegment(sketch, "E94.MirrorCS", {"start": v(-33, -90) * mm, "end": v(-15, -108) * mm});
            skLineSegment(sketch, "E95.MirrorCS", {"start": v(-15, -108) * mm, "end": v(-15, -120) * mm});
            skPoint(sketch, "E96.MirrorP", {"position": v(-3.45, -115.09) * mm});
            skSolve(sketch);
        }
        {
            var Q0;
            {var subQ0=sQuery(id+"F16.wireOp",EDGE,"E88.MirrorCS");Q0=makeQuery(id+"F16.imprint","IMPRINT",FACE,{"disambiguationData":[TD([[makeQuery(id+"F16.imprint","IMPRINT",EDGE,{"derivedFrom":subQ0}),1.0]])]});}
            var Q1;
            Q1=makeQuery(id+"F16.imprint","IMPRINT",FACE,{"disambiguationData":[TD([[makeQuery(id+"F16.imprint","IMPRINT",EDGE,{"derivedFrom":sQuery(id+"F16.wireOp",EDGE,"E79")}),-1.0]])]});
            var Q2;
            Q2=makeQuery(id+"F16.imprint","IMPRINT",FACE,{"disambiguationData":[TD([[makeQuery(id+"F16.imprint","IMPRINT",EDGE,{"derivedFrom":makeQuery(id+"F1.opExtrude","CAP_EDGE",EDGE,{"disambiguationData":[OSD([sQuery(id+"F0.wireOp",EDGE,"E1.left")])],"isStart":true})}),-1.0]])]});
            var Q3;
            Q3=makeQuery(id+"F2.opExtrude","CAP_FACE",FACE,{"disambiguationData":[OSD([sQuery(id+"F0.wireOp",EDGE,"E12"),sQuery(id+"F0.wireOp",EDGE,"E13"),sQuery(id+"F0.wireOp",EDGE,"E14"),sQuery(id+"F0.wireOp",EDGE,"E15"),sQuery(id+"F0.wireOp",EDGE,"E17.filletArc"),sQuery(id+"F0.wireOp",EDGE,"E18.filletArc"),sQuery(id+"F0.wireOp",EDGE,"E19.filletArc"),sQuery(id+"F0.wireOp",EDGE,"E20.filletArc"),sQuery(id+"F0.wireOp",EDGE,"E25.0"),sQuery(id+"F0.wireOp",EDGE,"E25.1"),sQuery(id+"F0.wireOp",EDGE,"E25.2"),sQuery(id+"F0.wireOp",EDGE,"E25.3"),sQuery(id+"F0.wireOp",EDGE,"E25.4"),sQuery(id+"F0.wireOp",EDGE,"E25.5"),sQuery(id+"F0.wireOp",EDGE,"E25.6"),sQuery(id+"F0.wireOp",EDGE,"E25.7")])],"isStart":false});
            extrude(context, id + "F17", {"entities" : qUnion([Q0, Q1, Q2]), "endBound" : BoundingType.UP_TO_SURFACE, "depth" : 25 * mm, "endBoundEntityFace" : qUnion([Q3]), "offsetDistance" : 25 * mm});
        }
    });
